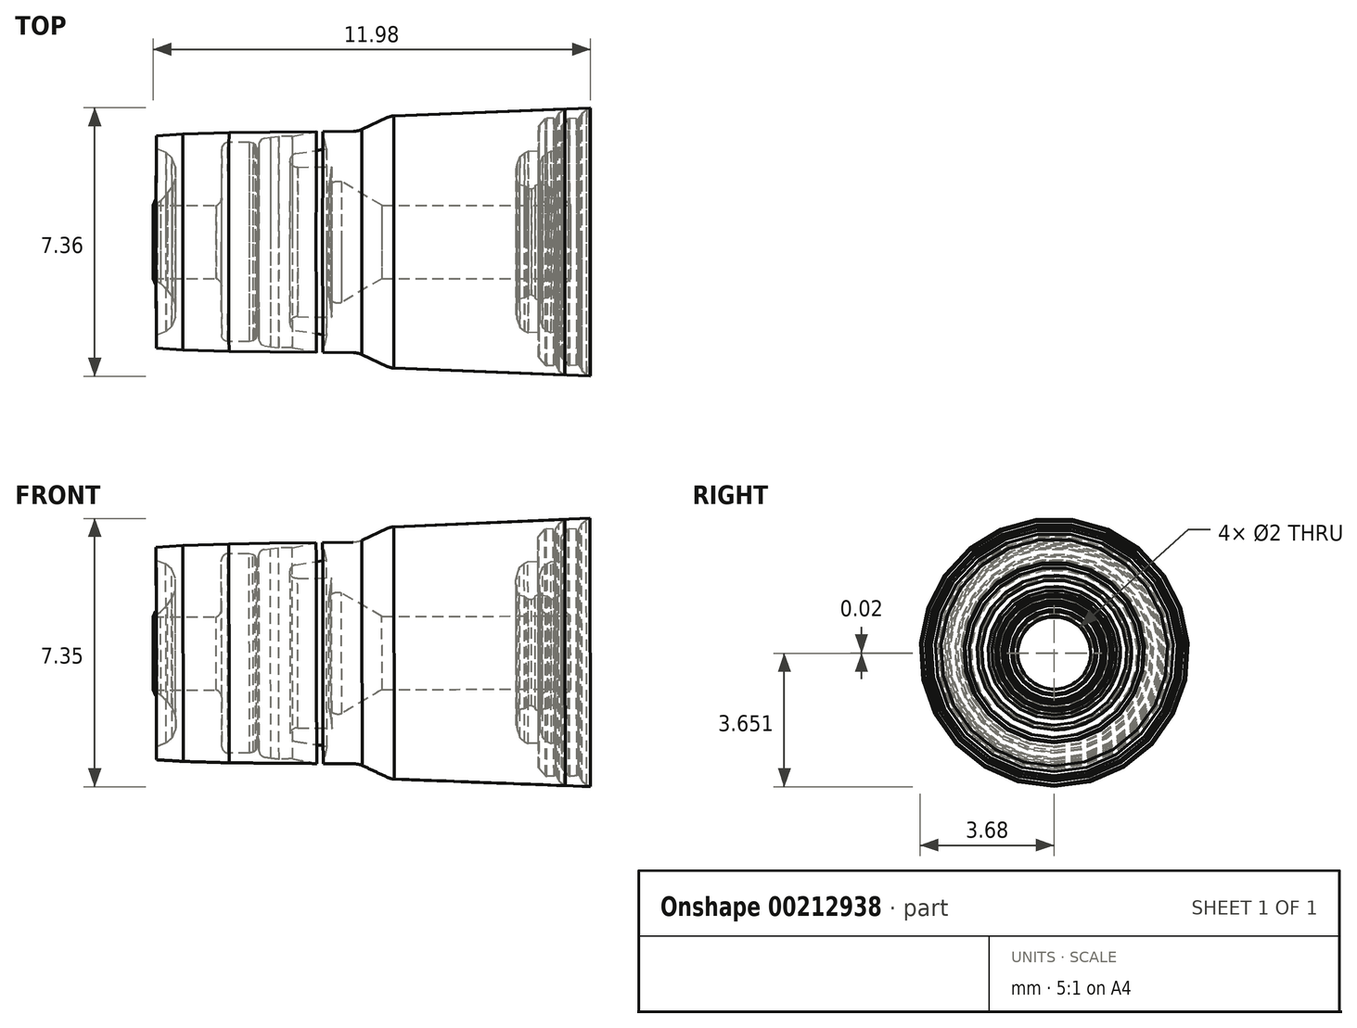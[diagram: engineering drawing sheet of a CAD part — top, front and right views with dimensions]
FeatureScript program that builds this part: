
annotation { "Feature Type Name" : "Feature", "Feature Type Description" : "" }
export const myFeature = defineFeature(function(context is Context, id is Id, definition is map)
    precondition{}
    {
        {
            var Q0;
            Q0=qCreatedBy(makeId("Front.planeOp"),FACE);
            var sketch = newSketch(context, id + "F0", { "sketchPlane" : qUnion([Q0])});
            skLineSegment(sketch, "E0", {"start": v(-44.43, 11.9) * mm, "end": v(-21.52, 11.96) * mm});
            skLineSegment(sketch, "E1", {"start": v(146.27, 12.37) * mm, "end": v(146.33, -14.1) * mm});
            skLineSegment(sketch, "E2", {"start": v(105.7, -14.27) * mm, "end": v(36.71, -14.55) * mm});
            skLineSegment(sketch, "E3", {"start": v(146.3, -0.86) * mm, "end": v(-44.43, -1.33) * mm, "construction": true});
            skArc(sketch, "E4", {"start": v(-42.35, -17.84) * mm, "mid": v(-43.1, -16.21) * mm, "end": v(-44.3, -14.89) * mm});
            skLineSegment(sketch, "E5", {"start": v(-42.35, -17.84) * mm, "end": v(-38.4, -17.83) * mm});
            skLineSegment(sketch, "E6", {"start": v(-38.4, -17.83) * mm, "end": v(-36.72, -19.51) * mm});
            skLineSegment(sketch, "E7", {"start": v(-36.72, -19.51) * mm, "end": v(-35.09, -28.11) * mm});
            skLineSegment(sketch, "E8", {"start": v(-35.09, -28.11) * mm, "end": v(-37.5, -32.1) * mm});
            skLineSegment(sketch, "E9", {"start": v(-37.5, -32.1) * mm, "end": v(-38.12, -32.6) * mm});
            skLineSegment(sketch, "E10", {"start": v(-38.12, -32.6) * mm, "end": v(-42.11, -32.86) * mm});
            skLineSegment(sketch, "E11", {"start": v(-42.11, -32.86) * mm, "end": v(-41.66, -39.75) * mm});
            skLineSegment(sketch, "E12", {"start": v(-41.66, -39.75) * mm, "end": v(-41.12, -40.16) * mm});
            skLineSegment(sketch, "E13", {"start": v(-41.12, -40.16) * mm, "end": v(-31.52, -40.77) * mm});
            skLineSegment(sketch, "E14", {"start": v(-31.52, -40.77) * mm, "end": v(-16.14, -40.93) * mm});
            skLineSegment(sketch, "E15", {"start": v(-16.14, -40.93) * mm, "end": v(14.46, -40.45) * mm});
            skLineSegment(sketch, "E16", {"start": v(30, -40.2) * mm, "end": v(30.61, -40.25) * mm});
            skLineSegment(sketch, "E17", {"start": v(30.61, -40.25) * mm, "end": v(41.38, -45.14) * mm});
            skLineSegment(sketch, "E18", {"start": v(41.38, -45.14) * mm, "end": v(42.29, -45.34) * mm});
            skLineSegment(sketch, "E19", {"start": v(42.29, -45.34) * mm, "end": v(42.83, -45.46) * mm});
            skLineSegment(sketch, "E20", {"start": v(42.83, -45.46) * mm, "end": v(105.8, -47.31) * mm});
            skLineSegment(sketch, "E21", {"start": v(105.8, -47.31) * mm, "end": v(112.34, -47.2) * mm});
            skArc(sketch, "E22", {"start": v(108.04, -43.16) * mm, "mid": v(109.44, -45.98) * mm, "end": v(112.34, -47.2) * mm});
            skArc(sketch, "E23", {"start": v(106.83, -44.64) * mm, "mid": v(107.62, -44.05) * mm, "end": v(108.04, -43.16) * mm});
            skArc(sketch, "E24", {"start": v(104.35, -44.2) * mm, "mid": v(105.55, -44.65) * mm, "end": v(106.83, -44.64) * mm});
            skArc(sketch, "E25", {"start": v(102.05, -40.33) * mm, "mid": v(102.13, -41) * mm, "end": v(102.55, -41.53) * mm});
            skLineSegment(sketch, "E26", {"start": v(102.55, -41.53) * mm, "end": v(104.35, -44.2) * mm});
            skLineSegment(sketch, "E27", {"start": v(102.05, -40.33) * mm, "end": v(102.05, -33.64) * mm});
            skLineSegment(sketch, "E28", {"start": v(102.05, -33.64) * mm, "end": v(96.34, -29.46) * mm});
            skArc(sketch, "E29", {"start": v(95.94, -18.2) * mm, "mid": v(94.61, -23.88) * mm, "end": v(96.34, -29.46) * mm});
            skArc(sketch, "E30", {"start": v(100.31, -18.67) * mm, "mid": v(98.22, -17.61) * mm, "end": v(95.94, -18.2) * mm});
            skArc(sketch, "E31", {"start": v(105.7, -14.27) * mm, "mid": v(103.68, -16.91) * mm, "end": v(103.57, -20.24) * mm});
            skLineSegment(sketch, "E32", {"start": v(100.31, -18.67) * mm, "end": v(103.57, -20.24) * mm});
            skLineSegment(sketch, "E33", {"start": v(24.46, -21.66) * mm, "end": v(36.71, -14.55) * mm});
            skArc(sketch, "E34", {"start": v(19.4, -19.3) * mm, "mid": v(21.31, -21.8) * mm, "end": v(24.46, -21.66) * mm});
            skLineSegment(sketch, "E35", {"start": v(-6.08, -31.57) * mm, "end": v(-6.1, -32.93) * mm});
            skLineSegment(sketch, "E36", {"start": v(-5.6, -35.2) * mm, "end": v(-6.08, -31.57) * mm});
            skLineSegment(sketch, "E37", {"start": v(6.68, -38.61) * mm, "end": v(-2.28, -38.3) * mm});
            skLineSegment(sketch, "E38", {"start": v(20.38, -26.98) * mm, "end": v(19.4, -19.3) * mm});
            skLineSegment(sketch, "E39", {"start": v(6.68, -28.04) * mm, "end": v(20.38, -26.98) * mm});
            skLineSegment(sketch, "E40", {"start": v(6.68, -30.15) * mm, "end": v(18.7, -33.92) * mm});
            skLineSegment(sketch, "E41", {"start": v(18.7, -33.92) * mm, "end": v(17.97, -40.4) * mm});
            skLineSegment(sketch, "E42", {"start": v(6.68, -38.61) * mm, "end": v(14.46, -40.45) * mm});
            skArc(sketch, "E43", {"start": v(6.68, -28.04) * mm, "mid": v(5.9, -29.1) * mm, "end": v(6.68, -30.15) * mm});
            skArc(sketch, "E44", {"start": v(-5.6, -35.2) * mm, "mid": v(-4.5, -37.35) * mm, "end": v(-2.28, -38.3) * mm});
            skArc(sketch, "E45", {"start": v(-9.61, -36.52) * mm, "mid": v(-7.24, -35.33) * mm, "end": v(-6.1, -32.93) * mm});
            skArc(sketch, "E46", {"start": v(-19.13, -34) * mm, "mid": v(-18.38, -35.9) * mm, "end": v(-16.5, -36.74) * mm});
            skLineSegment(sketch, "E47", {"start": v(-16.5, -36.74) * mm, "end": v(-9.61, -36.52) * mm});
            skLineSegment(sketch, "E48", {"start": v(-19.13, -34) * mm, "end": v(-19.34, -16.12) * mm});
            skArc(sketch, "E49", {"start": v(-19.34, -16.12) * mm, "mid": v(-19.82, -15.24) * mm, "end": v(-20.7, -14.8) * mm});
            skLineSegment(sketch, "E50.trimOffspring", {"start": v(-20.7, -14.8) * mm, "end": v(-44.3, -14.89) * mm});
            skLineSegment(sketch, "E51.trimOffspring", {"start": v(17.97, -40.4) * mm, "end": v(30, -40.2) * mm});
            skPoint(sketch, "E52.orphan", {"position": v(118.9, -47.1) * mm});
            skPoint(sketch, "E53.orphan", {"position": v(108.17, -41.53) * mm});
            skLineSegment(sketch, "E54", {"start": v(27.99, 38.96) * mm, "end": v(-2.22, 38.58) * mm});
            skLineSegment(sketch, "E55", {"start": v(-2.22, 38.58) * mm, "end": v(-16.99, 38.38) * mm});
            skLineSegment(sketch, "E56", {"start": v(-16.99, 38.38) * mm, "end": v(-33.63, 37.78) * mm});
            skLineSegment(sketch, "E57", {"start": v(-33.63, 37.78) * mm, "end": v(-43.3, 37.15) * mm});
            skLineSegment(sketch, "E58", {"start": v(-43.3, 37.15) * mm, "end": v(-43.3, 32.58) * mm});
            skLineSegment(sketch, "E59", {"start": v(-43.3, 32.58) * mm, "end": v(-43.14, 32.36) * mm});
            skLineSegment(sketch, "E60", {"start": v(-43.14, 32.36) * mm, "end": v(-39.76, 31.04) * mm});
            skLineSegment(sketch, "E61", {"start": v(-39.76, 31.04) * mm, "end": v(-37.69, 29.27) * mm});
            skLineSegment(sketch, "E62", {"start": v(-37.69, 29.27) * mm, "end": v(-36.34, 25.9) * mm});
            skLineSegment(sketch, "E63", {"start": v(-36.34, 25.9) * mm, "end": v(-36.34, 21.68) * mm});
            skLineSegment(sketch, "E64", {"start": v(-36.34, 21.68) * mm, "end": v(-37.4, 18.81) * mm});
            skLineSegment(sketch, "E65", {"start": v(-37.4, 18.81) * mm, "end": v(-39.2, 16.28) * mm});
            skLineSegment(sketch, "E66", {"start": v(-39.2, 16.28) * mm, "end": v(-41.62, 13.75) * mm});
            skLineSegment(sketch, "E67", {"start": v(-41.62, 13.75) * mm, "end": v(-42.79, 12.9) * mm});
            skLineSegment(sketch, "E68", {"start": v(-42.79, 12.9) * mm, "end": v(-43.54, 13.94) * mm});
            skLineSegment(sketch, "E69", {"start": v(-43.54, 13.94) * mm, "end": v(-44.43, 11.9) * mm});
            skLineSegment(sketch, "E70", {"start": v(-19.63, 32.44) * mm, "end": v(-19.63, 14.76) * mm});
            skLineSegment(sketch, "E71", {"start": v(-17.4, 34.87) * mm, "end": v(-9.61, 34.87) * mm});
            skLineSegment(sketch, "E72", {"start": v(-9.61, 34.87) * mm, "end": v(-8.22, 34.51) * mm});
            skLineSegment(sketch, "E73", {"start": v(-8.22, 34.51) * mm, "end": v(-7.43, 33.92) * mm});
            skLineSegment(sketch, "E74", {"start": v(-7.43, 33.92) * mm, "end": v(-6.99, 32.8) * mm});
            skLineSegment(sketch, "E75", {"start": v(-6.99, 32.8) * mm, "end": v(-6.55, 28.87) * mm});
            skLineSegment(sketch, "E76", {"start": v(-6.55, 28.87) * mm, "end": v(-6.2, 33.88) * mm});
            skLineSegment(sketch, "E77", {"start": v(-4.15, 36.36) * mm, "end": v(-1.92, 36.7) * mm});
            skLineSegment(sketch, "E78", {"start": v(-1.92, 36.7) * mm, "end": v(1.03, 37.05) * mm});
            skLineSegment(sketch, "E79", {"start": v(1.03, 37.05) * mm, "end": v(5.97, 37.05) * mm});
            skLineSegment(sketch, "E80", {"start": v(5.97, 37.05) * mm, "end": v(14.64, 38.79) * mm});
            skLineSegment(sketch, "E81", {"start": v(16.98, 38.82) * mm, "end": v(18.38, 32.56) * mm});
            skLineSegment(sketch, "E82", {"start": v(18.38, 32.56) * mm, "end": v(7.15, 30.79) * mm});
            skLineSegment(sketch, "E83", {"start": v(7.92, 25.9) * mm, "end": v(20.24, 26.05) * mm});
            skLineSegment(sketch, "E84", {"start": v(20.24, 26.05) * mm, "end": v(19.92, 22.83) * mm});
            skLineSegment(sketch, "E85", {"start": v(19.92, 22.83) * mm, "end": v(19.21, 18.84) * mm});
            skLineSegment(sketch, "E86", {"start": v(19.21, 18.84) * mm, "end": v(20.13, 20.1) * mm});
            skArc(sketch, "E87", {"start": v(-17.4, 34.87) * mm, "mid": v(-18.99, 34.1) * mm, "end": v(-19.63, 32.44) * mm});
            skArc(sketch, "E88", {"start": v(-4.15, 36.36) * mm, "mid": v(-5.65, 35.51) * mm, "end": v(-6.2, 33.88) * mm});
            skArc(sketch, "E89", {"start": v(7.15, 30.79) * mm, "mid": v(5.1, 27.96) * mm, "end": v(7.92, 25.9) * mm});
            skArc(sketch, "E90", {"start": v(23.81, 20.67) * mm, "mid": v(21.9, 20.85) * mm, "end": v(20.13, 20.1) * mm});
            skArc(sketch, "E91", {"start": v(-21.52, 11.96) * mm, "mid": v(-20.14, 13.07) * mm, "end": v(-19.63, 14.76) * mm});
            skArc(sketch, "E92", {"start": v(27.99, 38.96) * mm, "mid": v(29.6, 39.13) * mm, "end": v(31.14, 39.59) * mm});
            skArc(sketch, "E93", {"start": v(42.72, 44.56) * mm, "mid": v(41.51, 44.38) * mm, "end": v(40.36, 43.97) * mm});
            skLineSegment(sketch, "E94", {"start": v(31.14, 39.59) * mm, "end": v(40.36, 43.97) * mm});
            skLineSegment(sketch, "E95", {"start": v(42.72, 44.56) * mm, "end": v(113.71, 47.64) * mm});
            skLineSegment(sketch, "E96", {"start": v(113.71, 47.64) * mm, "end": v(112.42, 47.03) * mm});
            skLineSegment(sketch, "E97", {"start": v(112.42, 47.03) * mm, "end": v(111.4, 46.24) * mm});
            skLineSegment(sketch, "E98", {"start": v(111.4, 46.24) * mm, "end": v(110.73, 45.7) * mm});
            skLineSegment(sketch, "E99", {"start": v(110.73, 45.7) * mm, "end": v(110.23, 44.76) * mm});
            skLineSegment(sketch, "E100", {"start": v(110.23, 44.76) * mm, "end": v(109.68, 43.66) * mm});
            skLineSegment(sketch, "E101", {"start": v(109.68, 43.66) * mm, "end": v(109.44, 42.2) * mm});
            skLineSegment(sketch, "E102", {"start": v(109.44, 42.2) * mm, "end": v(109.53, 40.14) * mm});
            skLineSegment(sketch, "E103", {"start": v(109.53, 40.14) * mm, "end": v(109.33, 40.19) * mm});
            skLineSegment(sketch, "E104", {"start": v(109.33, 40.19) * mm, "end": v(108.8, 43.76) * mm});
            skLineSegment(sketch, "E105", {"start": v(108.8, 43.76) * mm, "end": v(106.25, 43.8) * mm});
            skLineSegment(sketch, "E106", {"start": v(106.25, 43.8) * mm, "end": v(105.78, 43.7) * mm});
            skLineSegment(sketch, "E107", {"start": v(105.78, 43.7) * mm, "end": v(103.6, 41.16) * mm});
            skLineSegment(sketch, "E108", {"start": v(103.6, 41.16) * mm, "end": v(103.27, 40.7) * mm});
            skLineSegment(sketch, "E109", {"start": v(103.27, 40.7) * mm, "end": v(103.27, 31.77) * mm});
            skLineSegment(sketch, "E110", {"start": v(103.27, 31.77) * mm, "end": v(99.61, 31.94) * mm});
            skLineSegment(sketch, "E111", {"start": v(99.61, 31.94) * mm, "end": v(98.27, 31.3) * mm});
            skLineSegment(sketch, "E112", {"start": v(98.27, 31.3) * mm, "end": v(96.57, 29.88) * mm});
            skLineSegment(sketch, "E113", {"start": v(96.57, 29.88) * mm, "end": v(95.63, 27.08) * mm});
            skLineSegment(sketch, "E114", {"start": v(95.63, 27.08) * mm, "end": v(95.26, 25.3) * mm});
            skLineSegment(sketch, "E115", {"start": v(95.26, 25.3) * mm, "end": v(95.36, 23) * mm});
            skLineSegment(sketch, "E116", {"start": v(95.36, 23) * mm, "end": v(95.53, 21.65) * mm});
            skLineSegment(sketch, "E117", {"start": v(95.53, 21.65) * mm, "end": v(96.31, 19.62) * mm});
            skLineSegment(sketch, "E118", {"start": v(96.31, 19.62) * mm, "end": v(98.38, 19.3) * mm});
            skLineSegment(sketch, "E119", {"start": v(98.38, 19.3) * mm, "end": v(98.95, 18.81) * mm});
            skLineSegment(sketch, "E120", {"start": v(98.95, 18.81) * mm, "end": v(99.78, 18.22) * mm});
            skLineSegment(sketch, "E121", {"start": v(99.78, 18.22) * mm, "end": v(100.87, 18.17) * mm});
            skLineSegment(sketch, "E122", {"start": v(100.87, 18.17) * mm, "end": v(102.13, 18.77) * mm});
            skLineSegment(sketch, "E123", {"start": v(102.13, 18.77) * mm, "end": v(102.16, 19.51) * mm});
            skLineSegment(sketch, "E124", {"start": v(102.16, 19.51) * mm, "end": v(103.27, 20.04) * mm});
            skLineSegment(sketch, "E125", {"start": v(103.27, 20.04) * mm, "end": v(104.01, 20.3) * mm});
            skLineSegment(sketch, "E126", {"start": v(104.01, 20.3) * mm, "end": v(104.47, 20.3) * mm});
            skLineSegment(sketch, "E127", {"start": v(104.47, 20.3) * mm, "end": v(104.13, 19.4) * mm});
            skLineSegment(sketch, "E128", {"start": v(104.13, 19.4) * mm, "end": v(103.8, 17.88) * mm});
            skLineSegment(sketch, "E129", {"start": v(103.8, 17.88) * mm, "end": v(103.8, 16.92) * mm});
            skLineSegment(sketch, "E130", {"start": v(103.8, 16.92) * mm, "end": v(104.01, 16.1) * mm});
            skLineSegment(sketch, "E131", {"start": v(104.01, 16.1) * mm, "end": v(104.5, 14.59) * mm});
            skLineSegment(sketch, "E132", {"start": v(104.5, 14.59) * mm, "end": v(104.78, 13.98) * mm});
            skLineSegment(sketch, "E133", {"start": v(104.78, 13.98) * mm, "end": v(105.56, 13.3) * mm});
            skLineSegment(sketch, "E134", {"start": v(105.56, 13.3) * mm, "end": v(106.26, 12.7) * mm});
            skLineSegment(sketch, "E135", {"start": v(106.26, 12.7) * mm, "end": v(106.76, 12.27) * mm});
            skLineSegment(sketch, "E136", {"start": v(23.81, 20.67) * mm, "end": v(38.45, 12.1) * mm});
            skLineSegment(sketch, "E137.trimOffspring", {"start": v(38.45, 12.1) * mm, "end": v(106.76, 12.27) * mm});
            skSolve(sketch);
        }
        {
            var Q0;
            Q0=makeQuery(id+"F0.imprint","IMPRINT",FACE,{"disambiguationData":[TD([[makeQuery(id+"F0.imprint","IMPRINT",EDGE,{"derivedFrom":sQuery(id+"F0.wireOp",EDGE,"E0")}),1.0]])]});
            var Q1;
            {var subQ1=sQuery(id+"F0.wireOp",EDGE,"E81");Q1=makeQuery(id+"F0.imprint","IMPRINT",FACE,{"disambiguationData":[TD([[makeQuery(id+"F0.imprint","IMPRINT",EDGE,{"derivedFrom":subQ1}),1.0]])]});}
            var Q2;
            Q2=sQuery(id+"F0.wireOp",EDGE,"E3");
            revolve(context, id + "F1", {"surfaceOperationType" : NewSurfaceOperationType.NEW, "entities" : qUnion([Q0, Q1]), "axis" : qUnion([Q2]), "revolveType" : RevolveType.FULL});
        }
        {
            var Q0;
            Q0=makeQuery(id+"F1.opRevolve","SWEPT_BODY",BODY,{"disambiguationData":[OSD([sQuery(id+"F0.wireOp",EDGE,"E0"),sQuery(id+"F0.wireOp",EDGE,"E54"),sQuery(id+"F0.wireOp",EDGE,"E55"),sQuery(id+"F0.wireOp",EDGE,"E56"),sQuery(id+"F0.wireOp",EDGE,"E57"),sQuery(id+"F0.wireOp",EDGE,"E58"),sQuery(id+"F0.wireOp",EDGE,"E59"),sQuery(id+"F0.wireOp",EDGE,"E60"),sQuery(id+"F0.wireOp",EDGE,"E61"),sQuery(id+"F0.wireOp",EDGE,"E62"),sQuery(id+"F0.wireOp",EDGE,"E63"),sQuery(id+"F0.wireOp",EDGE,"E64"),sQuery(id+"F0.wireOp",EDGE,"E65"),sQuery(id+"F0.wireOp",EDGE,"E66"),sQuery(id+"F0.wireOp",EDGE,"E67"),sQuery(id+"F0.wireOp",EDGE,"E68"),sQuery(id+"F0.wireOp",EDGE,"E69"),sQuery(id+"F0.wireOp",EDGE,"E70"),sQuery(id+"F0.wireOp",EDGE,"E71"),sQuery(id+"F0.wireOp",EDGE,"E72"),sQuery(id+"F0.wireOp",EDGE,"E73"),sQuery(id+"F0.wireOp",EDGE,"E74"),sQuery(id+"F0.wireOp",EDGE,"E75"),sQuery(id+"F0.wireOp",EDGE,"E76"),sQuery(id+"F0.wireOp",EDGE,"E77"),sQuery(id+"F0.wireOp",EDGE,"E78"),sQuery(id+"F0.wireOp",EDGE,"E79"),sQuery(id+"F0.wireOp",EDGE,"E80"),sQuery(id+"F0.wireOp",EDGE,"E87"),sQuery(id+"F0.wireOp",EDGE,"E88"),sQuery(id+"F0.wireOp",EDGE,"E91")])]});
            var Q1;
            Q1=makeQuery(id+"F1.opRevolve","SWEPT_BODY",BODY,{"disambiguationData":[OSD([sQuery(id+"F0.wireOp",EDGE,"E54"),sQuery(id+"F0.wireOp",EDGE,"E81"),sQuery(id+"F0.wireOp",EDGE,"E82"),sQuery(id+"F0.wireOp",EDGE,"E83"),sQuery(id+"F0.wireOp",EDGE,"E84"),sQuery(id+"F0.wireOp",EDGE,"E85"),sQuery(id+"F0.wireOp",EDGE,"E86"),sQuery(id+"F0.wireOp",EDGE,"E89"),sQuery(id+"F0.wireOp",EDGE,"E90"),sQuery(id+"F0.wireOp",EDGE,"E92"),sQuery(id+"F0.wireOp",EDGE,"E93"),sQuery(id+"F0.wireOp",EDGE,"E94"),sQuery(id+"F0.wireOp",EDGE,"E95"),sQuery(id+"F0.wireOp",EDGE,"E96"),sQuery(id+"F0.wireOp",EDGE,"E97"),sQuery(id+"F0.wireOp",EDGE,"E98"),sQuery(id+"F0.wireOp",EDGE,"E99"),sQuery(id+"F0.wireOp",EDGE,"E100"),sQuery(id+"F0.wireOp",EDGE,"E101"),sQuery(id+"F0.wireOp",EDGE,"E102"),sQuery(id+"F0.wireOp",EDGE,"E103"),sQuery(id+"F0.wireOp",EDGE,"E104"),sQuery(id+"F0.wireOp",EDGE,"E105"),sQuery(id+"F0.wireOp",EDGE,"E106"),sQuery(id+"F0.wireOp",EDGE,"E107"),sQuery(id+"F0.wireOp",EDGE,"E108"),sQuery(id+"F0.wireOp",EDGE,"E109"),sQuery(id+"F0.wireOp",EDGE,"E110"),sQuery(id+"F0.wireOp",EDGE,"E111"),sQuery(id+"F0.wireOp",EDGE,"E112"),sQuery(id+"F0.wireOp",EDGE,"E113"),sQuery(id+"F0.wireOp",EDGE,"E114"),sQuery(id+"F0.wireOp",EDGE,"E115"),sQuery(id+"F0.wireOp",EDGE,"E116"),sQuery(id+"F0.wireOp",EDGE,"E117"),sQuery(id+"F0.wireOp",EDGE,"E118"),sQuery(id+"F0.wireOp",EDGE,"E119"),sQuery(id+"F0.wireOp",EDGE,"E120"),sQuery(id+"F0.wireOp",EDGE,"E121"),sQuery(id+"F0.wireOp",EDGE,"E122"),sQuery(id+"F0.wireOp",EDGE,"E123"),sQuery(id+"F0.wireOp",EDGE,"E124"),sQuery(id+"F0.wireOp",EDGE,"E125"),sQuery(id+"F0.wireOp",EDGE,"E126"),sQuery(id+"F0.wireOp",EDGE,"E127"),sQuery(id+"F0.wireOp",EDGE,"E128"),sQuery(id+"F0.wireOp",EDGE,"E129"),sQuery(id+"F0.wireOp",EDGE,"E130"),sQuery(id+"F0.wireOp",EDGE,"E131"),sQuery(id+"F0.wireOp",EDGE,"E132"),sQuery(id+"F0.wireOp",EDGE,"E133"),sQuery(id+"F0.wireOp",EDGE,"E134"),sQuery(id+"F0.wireOp",EDGE,"E135"),sQuery(id+"F0.wireOp",EDGE,"E136"),sQuery(id+"F0.wireOp",EDGE,"E137.trimOffspring")])]});
            var Q2;
            Q2=qCreatedBy(makeId("Origin.pointOp"),VERTEX);
            transform(context, id + "F2", {"entities" : qUnion([Q0, Q1]), "transformType" : TransformType.SCALE_UNIFORMLY, "scale" : 0.08, "scalePoint" : qUnion([Q2]), "makeCopy" : false});
        }
        {
            var Q0;
            Q0=qCreatedBy(makeId("Front.planeOp"),FACE);
            var sketch = newSketch(context, id + "F3", { "sketchPlane" : qUnion([Q0])});
            skLineSegment(sketch, "E138", {"start": v(3.23, 3.37) * mm, "end": v(7.91, 3.57) * mm});
            skArc(sketch, "E139", {"start": v(3.23, 3.37) * mm, "mid": v(3.14, 3.36) * mm, "end": v(3.05, 3.33) * mm});
            skLineSegment(sketch, "E140", {"start": v(2.36, 3) * mm, "end": v(3.05, 3.33) * mm});
            skArc(sketch, "E141", {"start": v(2.12, 2.95) * mm, "mid": v(2.24, 2.96) * mm, "end": v(2.36, 3) * mm});
            skLineSegment(sketch, "E142", {"start": v(1.28, 2.94) * mm, "end": v(2.12, 2.95) * mm});
            skLineSegment(sketch, "E143", {"start": v(1.28, 2.94) * mm, "end": v(1.4, 2.46) * mm});
            skLineSegment(sketch, "E144", {"start": v(0.54, 2.33) * mm, "end": v(1.4, 2.46) * mm});
            skLineSegment(sketch, "E145", {"start": v(0.38, 2.14) * mm, "end": v(0.4, -2.33) * mm, "construction": true});
            skLineSegment(sketch, "E146", {"start": v(0.6, 1.96) * mm, "end": v(1.53, 1.97) * mm});
            skLineSegment(sketch, "E147", {"start": v(1.5, 1.73) * mm, "end": v(1.53, 1.97) * mm});
            skLineSegment(sketch, "E148", {"start": v(1.45, 1.43) * mm, "end": v(1.5, 1.73) * mm});
            skLineSegment(sketch, "E149", {"start": v(1.45, 1.43) * mm, "end": v(1.52, 1.52) * mm});
            skArc(sketch, "E150", {"start": v(1.8, 1.56) * mm, "mid": v(1.66, 1.58) * mm, "end": v(1.52, 1.52) * mm});
            skLineSegment(sketch, "E151", {"start": v(1.8, 1.56) * mm, "end": v(2.9, 0.92) * mm});
            skLineSegment(sketch, "E152", {"start": v(2.9, 0.92) * mm, "end": v(7.45, 0.93) * mm});
            skLineSegment(sketch, "E153", {"start": v(-3.28, 2.81) * mm, "end": v(-2.54, 2.86) * mm});
            skLineSegment(sketch, "E154", {"start": v(7.88, 3.56) * mm, "end": v(7.91, 3.57) * mm});
            skLineSegment(sketch, "E155", {"start": v(7.8, 3.5) * mm, "end": v(7.88, 3.56) * mm});
            skLineSegment(sketch, "E156.0", {"start": v(8.38, 3.46) * mm, "end": v(8.4, -3.6) * mm, "construction": true});
            skLineSegment(sketch, "E157", {"start": v(7.75, 3.46) * mm, "end": v(7.8, 3.5) * mm});
            skLineSegment(sketch, "E158", {"start": v(7.71, 3.39) * mm, "end": v(7.75, 3.46) * mm});
            skLineSegment(sketch, "E159", {"start": v(7.67, 3.3) * mm, "end": v(7.71, 3.39) * mm});
            skLineSegment(sketch, "E160", {"start": v(7.65, 3.2) * mm, "end": v(7.67, 3.3) * mm});
            skLineSegment(sketch, "E161", {"start": v(7.65, 3.04) * mm, "end": v(7.66, 3.04) * mm});
            skLineSegment(sketch, "E162", {"start": v(7.6, 3.31) * mm, "end": v(7.65, 3.04) * mm});
            skLineSegment(sketch, "E163", {"start": v(7.65, 3.2) * mm, "end": v(7.66, 3.04) * mm});
            skLineSegment(sketch, "E164", {"start": v(7.41, 3.31) * mm, "end": v(7.6, 3.31) * mm});
            skLineSegment(sketch, "E165", {"start": v(7.38, 3.3) * mm, "end": v(7.41, 3.31) * mm});
            skLineSegment(sketch, "E166", {"start": v(7.21, 3.11) * mm, "end": v(7.38, 3.3) * mm});
            skLineSegment(sketch, "E167", {"start": v(7.19, 3.08) * mm, "end": v(7.21, 3.11) * mm});
            skLineSegment(sketch, "E168", {"start": v(6.91, 2.42) * mm, "end": v(7.19, 2.4) * mm});
            skLineSegment(sketch, "E169", {"start": v(6.8, 2.37) * mm, "end": v(6.91, 2.42) * mm});
            skLineSegment(sketch, "E170", {"start": v(6.68, 2.26) * mm, "end": v(6.8, 2.37) * mm});
            skLineSegment(sketch, "E171", {"start": v(6.6, 2.05) * mm, "end": v(6.68, 2.26) * mm});
            skLineSegment(sketch, "E172", {"start": v(6.58, 1.91) * mm, "end": v(6.6, 2.05) * mm});
            skLineSegment(sketch, "E173", {"start": v(7, 1.38) * mm, "end": v(7.1, 1.42) * mm});
            skLineSegment(sketch, "E174", {"start": v(6.92, 1.38) * mm, "end": v(7, 1.38) * mm});
            skLineSegment(sketch, "E175.0", {"start": v(-3.28, 2.81) * mm, "end": v(-3.26, -3.01) * mm, "construction": true});
            skLineSegment(sketch, "E176", {"start": v(7.19, 2.4) * mm, "end": v(7.19, 3.08) * mm});
            skLineSegment(sketch, "E177", {"start": v(6.58, 1.91) * mm, "end": v(6.59, 1.74) * mm});
            skLineSegment(sketch, "E178", {"start": v(6.59, 1.74) * mm, "end": v(6.6, 1.64) * mm});
            skLineSegment(sketch, "E179", {"start": v(6.6, 1.64) * mm, "end": v(6.66, 1.48) * mm});
            skLineSegment(sketch, "E180", {"start": v(6.66, 1.48) * mm, "end": v(6.82, 1.46) * mm});
            skLineSegment(sketch, "E181", {"start": v(6.82, 1.46) * mm, "end": v(6.86, 1.42) * mm});
            skLineSegment(sketch, "E182", {"start": v(6.86, 1.42) * mm, "end": v(6.92, 1.38) * mm});
            skLineSegment(sketch, "E183", {"start": v(7.1, 1.48) * mm, "end": v(7.19, 1.52) * mm});
            skLineSegment(sketch, "E184", {"start": v(7.19, 1.52) * mm, "end": v(7.24, 1.54) * mm});
            skLineSegment(sketch, "E185", {"start": v(7.24, 1.54) * mm, "end": v(7.28, 1.54) * mm});
            skLineSegment(sketch, "E186", {"start": v(7.25, 1.47) * mm, "end": v(7.28, 1.54) * mm});
            skLineSegment(sketch, "E187", {"start": v(7.1, 1.42) * mm, "end": v(7.1, 1.48) * mm});
            skLineSegment(sketch, "E188", {"start": v(7.23, 1.35) * mm, "end": v(7.25, 1.47) * mm});
            skLineSegment(sketch, "E189", {"start": v(7.23, 1.28) * mm, "end": v(7.24, 1.22) * mm});
            skLineSegment(sketch, "E190", {"start": v(7.24, 1.22) * mm, "end": v(7.28, 1.1) * mm});
            skLineSegment(sketch, "E191", {"start": v(7.28, 1.1) * mm, "end": v(7.3, 1.06) * mm});
            skLineSegment(sketch, "E192", {"start": v(7.3, 1.06) * mm, "end": v(7.45, 0.93) * mm});
            skLineSegment(sketch, "E193", {"start": v(0.45, 2.8) * mm, "end": v(1.1, 2.93) * mm});
            skLineSegment(sketch, "E194", {"start": v(0.08, 2.8) * mm, "end": v(0.45, 2.8) * mm});
            skLineSegment(sketch, "E195", {"start": v(-0.15, 2.78) * mm, "end": v(0.08, 2.8) * mm});
            skLineSegment(sketch, "E196", {"start": v(-0.31, 2.75) * mm, "end": v(-0.15, 2.78) * mm});
            skLineSegment(sketch, "E197", {"start": v(-0.47, 2.57) * mm, "end": v(-0.46, -2.76) * mm, "construction": true});
            skArc(sketch, "E198", {"start": v(-0.47, 2.57) * mm, "mid": v(-0.47, 2.57) * mm, "end": v(-0.47, 2.56) * mm});
            skLineSegment(sketch, "E199", {"start": v(-0.53, 2.48) * mm, "end": v(-0.5, 2.18) * mm});
            skLineSegment(sketch, "E200", {"start": v(-0.56, 2.57) * mm, "end": v(-0.53, 2.48) * mm});
            skLineSegment(sketch, "E201", {"start": v(-0.62, 2.61) * mm, "end": v(-0.56, 2.57) * mm});
            skLineSegment(sketch, "E202", {"start": v(-0.73, 2.64) * mm, "end": v(-0.62, 2.61) * mm});
            skLineSegment(sketch, "E203", {"start": v(-1.32, 2.64) * mm, "end": v(-0.73, 2.64) * mm});
            skArc(sketch, "E204", {"start": v(-1.32, 2.64) * mm, "mid": v(-1.44, 2.58) * mm, "end": v(-1.49, 2.45) * mm});
            skLineSegment(sketch, "E205", {"start": v(-1.49, 1.12) * mm, "end": v(-1.49, 2.45) * mm});
            skArc(sketch, "E206", {"start": v(-1.63, 0.9) * mm, "mid": v(-1.52, 0.99) * mm, "end": v(-1.49, 1.12) * mm});
            skLineSegment(sketch, "E207", {"start": v(-3.36, 0.9) * mm, "end": v(-1.63, 0.9) * mm});
            skLineSegment(sketch, "E208", {"start": v(-3.36, 0.9) * mm, "end": v(-3.3, 1.05) * mm});
            skLineSegment(sketch, "E209", {"start": v(-3.15, 1.04) * mm, "end": v(-2.97, 1.23) * mm});
            skLineSegment(sketch, "E210", {"start": v(-2.97, 1.23) * mm, "end": v(-2.83, 1.42) * mm});
            skLineSegment(sketch, "E211", {"start": v(-2.83, 1.42) * mm, "end": v(-2.75, 1.64) * mm});
            skLineSegment(sketch, "E212", {"start": v(-2.75, 1.64) * mm, "end": v(-2.75, 1.96) * mm});
            skLineSegment(sketch, "E213", {"start": v(-2.85, 2.21) * mm, "end": v(-2.75, 1.96) * mm});
            skLineSegment(sketch, "E214", {"start": v(-3, 2.35) * mm, "end": v(-2.85, 2.21) * mm});
            skLineSegment(sketch, "E215", {"start": v(-3.26, 2.45) * mm, "end": v(-3, 2.35) * mm});
            skLineSegment(sketch, "E216", {"start": v(-3.28, 2.46) * mm, "end": v(-3.26, 2.45) * mm});
            skLineSegment(sketch, "E217", {"start": v(-3.3, 1.05) * mm, "end": v(-3.24, 0.98) * mm});
            skLineSegment(sketch, "E218", {"start": v(-3.24, 0.98) * mm, "end": v(-3.15, 1.04) * mm});
            skLineSegment(sketch, "E219", {"start": v(8.6, 3.6) * mm, "end": v(8.62, -3.75) * mm, "construction": true});
            skLineSegment(sketch, "E220", {"start": v(8.61, -0.07) * mm, "end": v(-3.27, -0.1) * mm, "construction": true});
            skLineSegment(sketch, "E221", {"start": v(-2.54, 2.86) * mm, "end": v(-1.29, 2.9) * mm});
            skLineSegment(sketch, "E222", {"start": v(-1.29, 2.9) * mm, "end": v(-0.17, 2.92) * mm});
            skLineSegment(sketch, "E223", {"start": v(-0.17, 2.92) * mm, "end": v(1.1, 2.93) * mm});
            skArc(sketch, "E224", {"start": v(0.54, 2.33) * mm, "mid": v(0.39, 2.12) * mm, "end": v(0.6, 1.96) * mm});
            skLineSegment(sketch, "E225", {"start": v(-0.5, 2.18) * mm, "end": v(-0.47, 2.56) * mm});
            skArc(sketch, "E226", {"start": v(-0.31, 2.75) * mm, "mid": v(-0.43, 2.69) * mm, "end": v(-0.47, 2.56) * mm});
            skLineSegment(sketch, "E227.MirrorCS", {"start": v(1.3, -3.12) * mm, "end": v(2.13, -3.12) * mm, "construction": true});
            skLineSegment(sketch, "E228", {"start": v(7.23, 1.35) * mm, "end": v(7.23, 1.28) * mm});
            skLineSegment(sketch, "E229", {"start": v(-3.28, 2.46) * mm, "end": v(-3.28, 2.81) * mm});
            skLineSegment(sketch, "E230", {"start": v(7.59, 3.9) * mm, "end": v(7.26, 3.9) * mm, "construction": true});
            skSolve(sketch);
        }
        {
            var Q0;
            Q0=makeQuery(id+"F3.imprint","IMPRINT",FACE,{"disambiguationData":[TD([[makeQuery(id+"F3.imprint","IMPRINT",EDGE,{"derivedFrom":sQuery(id+"F3.wireOp",EDGE,"E138")}),-1.0]])]});
            var Q1;
            Q1=makeQuery(id+"F3.imprint","IMPRINT",FACE,{"disambiguationData":[TD([[makeQuery(id+"F3.imprint","IMPRINT",EDGE,{"derivedFrom":sQuery(id+"F3.wireOp",EDGE,"E153")}),-1.0]])]});
            var Q2;
            Q2=sQuery(id+"F3.wireOp",EDGE,"E220");
            revolve(context, id + "F4", {"surfaceOperationType" : NewSurfaceOperationType.NEW, "entities" : qUnion([Q0, Q1]), "axis" : qUnion([Q2]), "revolveType" : RevolveType.FULL});
        }
    });
